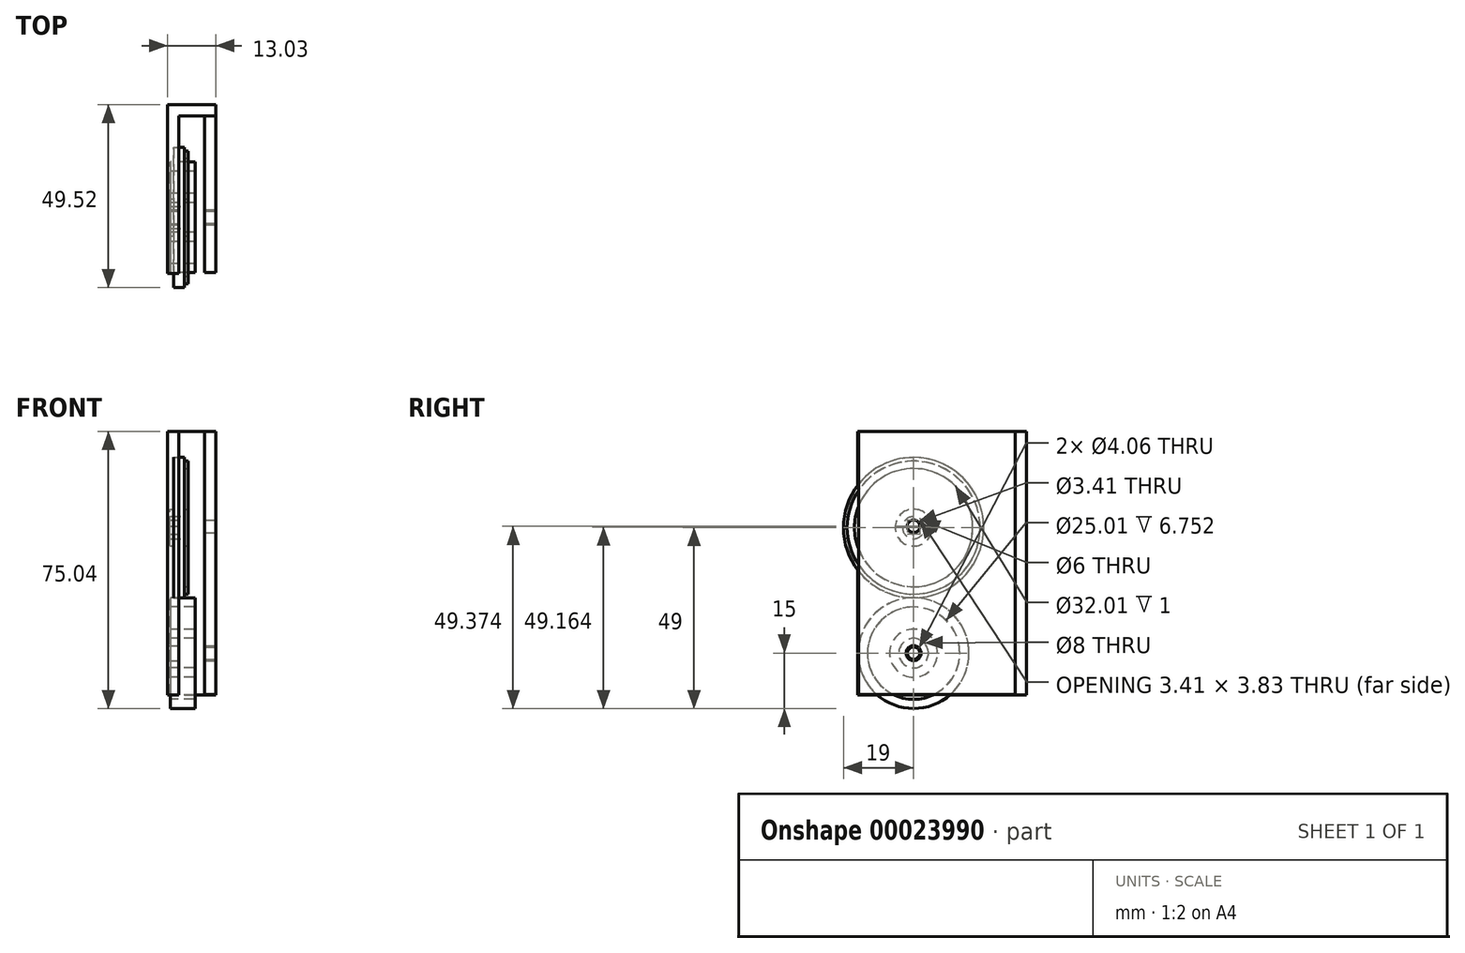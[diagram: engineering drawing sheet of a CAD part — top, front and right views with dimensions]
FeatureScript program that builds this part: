
annotation { "Feature Type Name" : "Feature", "Feature Type Description" : "" }
export const myFeature = defineFeature(function(context is Context, id is Id, definition is map)
    precondition{}
    {
        {
            var Q0;
            Q0=qCreatedBy(makeId("Front.planeOp"),FACE);
            var sketch = newSketch(context, id + "F0", { "sketchPlane" : qUnion([Q0])});
            skLineSegment(sketch, "E0", {"start": v(-10.94, 0) * mm, "end": v(9.84, 0) * mm, "construction": true});
            skLineSegment(sketch, "E1.bottom", {"start": v(-2.3, 4) * mm, "end": v(4.46, 4) * mm});
            skLineSegment(sketch, "E1.top", {"start": v(-2.3, 6.5) * mm, "end": v(4.46, 6.5) * mm});
            skLineSegment(sketch, "E1.left", {"start": v(-2.3, 4) * mm, "end": v(-2.3, 6.5) * mm});
            skLineSegment(sketch, "E1.right", {"start": v(4.46, 4) * mm, "end": v(4.46, 6.5) * mm});
            skLineSegment(sketch, "E2.bottom", {"start": v(-0.6, 6.5) * mm, "end": v(2.58, 6.5) * mm});
            skLineSegment(sketch, "E2.top", {"start": v(-0.6, 12.5) * mm, "end": v(2.58, 12.5) * mm});
            skLineSegment(sketch, "E2.left", {"start": v(-0.6, 6.5) * mm, "end": v(-0.6, 12.5) * mm});
            skLineSegment(sketch, "E2.right", {"start": v(2.58, 6.5) * mm, "end": v(2.58, 12.5) * mm});
            skLineSegment(sketch, "E3.bottom", {"start": v(4.46, 12.5) * mm, "end": v(-2.3, 12.5) * mm});
            skLineSegment(sketch, "E3.top", {"start": v(4.46, 15) * mm, "end": v(-2.3, 15) * mm});
            skLineSegment(sketch, "E3.left", {"start": v(4.46, 12.5) * mm, "end": v(4.46, 15) * mm});
            skLineSegment(sketch, "E3.right", {"start": v(-2.3, 12.5) * mm, "end": v(-2.3, 15) * mm});
            skLineSegment(sketch, "E4.right", {"start": v(2.58, 50) * mm, "end": v(2.58, 52) * mm});
            skLineSegment(sketch, "E5.left", {"start": v(-1.42, 39) * mm, "end": v(-1.42, 53) * mm});
            skLineSegment(sketch, "E5.right", {"start": v(1.58, 39) * mm, "end": v(1.58, 53) * mm});
            skLineSegment(sketch, "E4.bottom", {"start": v(-2.42, 50) * mm, "end": v(2.58, 50) * mm});
            skLineSegment(sketch, "E5.bottom", {"start": v(-1.42, 39) * mm, "end": v(1.58, 39) * mm});
            skLineSegment(sketch, "E6.top", {"start": v(-2.42, 37) * mm, "end": v(2.58, 37) * mm});
            skLineSegment(sketch, "E5.top", {"start": v(-1.42, 53) * mm, "end": v(1.58, 53) * mm});
            skLineSegment(sketch, "E4.top", {"start": v(-2.42, 52) * mm, "end": v(2.58, 52) * mm});
            skLineSegment(sketch, "E6.bottom", {"start": v(-2.42, 39) * mm, "end": v(2.58, 39) * mm});
            skLineSegment(sketch, "E6.right", {"start": v(2.58, 39) * mm, "end": v(2.58, 37) * mm});
            skLineSegment(sketch, "E6.left", {"start": v(-2.42, 39) * mm, "end": v(-2.42, 37) * mm});
            skLineSegment(sketch, "E4.left", {"start": v(-2.42, 50) * mm, "end": v(-2.42, 52) * mm});
            skLineSegment(sketch, "E7", {"start": v(-2.42, 34) * mm, "end": v(-17.57, 34) * mm});
            skSolve(sketch);
        }
        {
            var Q0;
            Q0=makeQuery(id+"F0.imprint","IMPRINT",FACE,{"disambiguationData":[TD([[makeQuery(id+"F0.imprint","IMPRINT",EDGE,{"derivedFrom":sQuery(id+"F0.wireOp",EDGE,"E2.bottom")}),1.0]])]});
            var Q1;
            Q1=makeQuery(id+"F0.imprint","IMPRINT",FACE,{"disambiguationData":[TD([[makeQuery(id+"F0.imprint","IMPRINT",EDGE,{"derivedFrom":sQuery(id+"F0.wireOp",EDGE,"E1.bottom")}),1.0]])]});
            var Q2;
            Q2=makeQuery(id+"F0.imprint","IMPRINT",FACE,{"disambiguationData":[TD([[makeQuery(id+"F0.imprint","IMPRINT",EDGE,{"derivedFrom":sQuery(id+"F0.wireOp",EDGE,"E3.top")}),1.0]])]});
            var Q3;
            Q3=sQuery(id+"F0.wireOp",EDGE,"E0");
            revolve(context, id + "F1", {"entities" : qUnion([Q0, Q1, Q2]), "axis" : qUnion([Q3]), "revolveType" : RevolveType.FULL});
        }
        {
            var Q0;
            Q0=makeQuery(id+"F0.imprint","IMPRINT",FACE,{"disambiguationData":[TD([[makeQuery(id+"F0.imprint","IMPRINT",EDGE,{"derivedFrom":sQuery(id+"F0.wireOp",EDGE,"E4.right")}),1.0]])]});
            var Q1;
            {var subQ2=sQuery(id+"F0.wireOp",EDGE,"E5.left");Q1=makeQuery(id+"F0.imprint","IMPRINT",FACE,{"disambiguationData":[TD([[makeQuery(id+"F0.imprint","IMPRINT",EDGE,{"derivedFrom":subQ2}),-1.0]])]});}
            var Q2;
            Q2=makeQuery(id+"F0.imprint","IMPRINT",FACE,{"disambiguationData":[TD([[makeQuery(id+"F0.imprint","IMPRINT",EDGE,{"derivedFrom":sQuery(id+"F0.wireOp",EDGE,"E6.top")}),1.0]])]});
            var Q3;
            Q3=sQuery(id+"F0.wireOp",EDGE,"E7");
            revolve(context, id + "F2", {"entities" : qUnion([Q0, Q1, Q2]), "axis" : qUnion([Q3]), "revolveType" : RevolveType.FULL});
        }
        {
            var Q0;
            Q0=qCreatedBy(makeId("Right.planeOp"),FACE);
            var sketch = newSketch(context, id + "F3", { "sketchPlane" : qUnion([Q0])});
            skLineSegment(sketch, "E8.bottom", {"start": v(-15.2, 60.04) * mm, "end": v(30.52, 60.04) * mm});
            skLineSegment(sketch, "E8.top", {"start": v(-15.2, -11.37) * mm, "end": v(30.52, -11.37) * mm});
            skLineSegment(sketch, "E8.left", {"start": v(-15.2, 60.04) * mm, "end": v(-15.2, -11.37) * mm});
            skLineSegment(sketch, "E8.right", {"start": v(30.52, 60.04) * mm, "end": v(30.52, -11.37) * mm});
            skCircle(sketch, "E9", {"center": v(0, 34) * mm, "radius": 1.75 * mm});
            skCircle(sketch, "E10", {"center": v(0, 0) * mm, "radius": 2 * mm});
            skSolve(sketch);
        }
        {
            var Q0;
            Q0 = qSketchRegion(id + "F3", true);
            extrude(context, id + "F4", {"entities" : qUnion([Q0]), "oppositeDirection" : true, "depth" : 3 * mm});
        }
        {
            var Q0;
            Q0=makeQuery(id+"F4.opExtrude","CAP_FACE",FACE,{"disambiguationData":[OSD([sQuery(id+"F3.wireOp",EDGE,"E8.bottom"),sQuery(id+"F3.wireOp",EDGE,"E8.top"),sQuery(id+"F3.wireOp",EDGE,"E8.left"),sQuery(id+"F3.wireOp",EDGE,"E8.right"),sQuery(id+"F3.wireOp",EDGE,"E9"),sQuery(id+"F3.wireOp",EDGE,"E10")])],"isStart":true});
            var sketch = newSketch(context, id + "F5", { "sketchPlane" : qUnion([Q0])});
            skLineSegment(sketch, "E11.bottom", {"start": v(27.52, -11.37) * mm, "end": v(30.52, -11.37) * mm});
            skLineSegment(sketch, "E11.top", {"start": v(27.52, 60.04) * mm, "end": v(30.52, 60.04) * mm});
            skLineSegment(sketch, "E11.left", {"start": v(27.52, -11.37) * mm, "end": v(27.52, 60.04) * mm});
            skLineSegment(sketch, "E11.right", {"start": v(30.52, -11.37) * mm, "end": v(30.52, 60.04) * mm});
            skSolve(sketch);
        }
        {
            var Q0;
            Q0 = qSketchRegion(id + "F5", true);
            extrude(context, id + "F6", {"entities" : qUnion([Q0]), "operationType" : NewBodyOperationType.ADD, "depth" : 10 * mm});
        }
        {
            var Q0;
            Q0=makeQuery(id+"F6.boolean.opBoolean","MERGE",FACE,{"derivedFrom":[makeQuery(id+"F4.opExtrude","SWEPT_FACE",FACE,{"disambiguationData":[OSD([sQuery(id+"F3.wireOp",EDGE,"E8.bottom")])]}),makeQuery(id+"F6.opExtrude","SWEPT_FACE",FACE,{"disambiguationData":[OSD([sQuery(id+"F5.wireOp",EDGE,"E11.top")])]})]});
            var sketch = newSketch(context, id + "F7", { "sketchPlane" : qUnion([Q0])});
            skPoint(sketch, "E12.0", {"position": v(10, 30.52) * mm});
            skPoint(sketch, "E13.0", {"position": v(10, 27.52) * mm});
            skLineSegment(sketch, "E14.bottom", {"start": v(7.03, -14.93) * mm, "end": v(10.03, -14.93) * mm});
            skLineSegment(sketch, "E14.top", {"start": v(7.03, 27.48) * mm, "end": v(10.03, 27.48) * mm});
            skLineSegment(sketch, "E14.left", {"start": v(7.03, -14.93) * mm, "end": v(7.03, 27.48) * mm});
            skLineSegment(sketch, "E14.right", {"start": v(10.03, -14.93) * mm, "end": v(10.03, 27.48) * mm});
            skSolve(sketch);
        }
        {
            var Q0;
            Q0 = qSketchRegion(id + "F7", true);
            extrude(context, id + "F8", {"entities" : qUnion([Q0]), "operationType" : NewBodyOperationType.ADD, "oppositeDirection" : true, "depth" : 71.2 * mm});
        }
        {
            var Q0;
            Q0=makeQuery(id+"F8.opExtrude","SWEPT_FACE",FACE,{"disambiguationData":[OSD([sQuery(id+"F7.wireOp",EDGE,"E14.right")])]});
            var sketch = newSketch(context, id + "F9", { "sketchPlane" : qUnion([Q0])});
            skCircle(sketch, "E15", {"center": v(0, 0) * mm, "radius": 1.66 * mm});
            skCircle(sketch, "E16", {"center": v(0, 0) * mm, "radius": 2.03 * mm});
            skCircle(sketch, "E17", {"center": v(0, 34.37) * mm, "radius": 1.7 * mm});
            skSolve(sketch);
        }
        {
            var Q0;
            Q0 = qSketchRegion(id + "F9", true);
            extrude(context, id + "F10", {"entities" : qUnion([Q0]), "operationType" : NewBodyOperationType.REMOVE, "oppositeDirection" : true, "depth" : 25 * mm});
        }
    });
